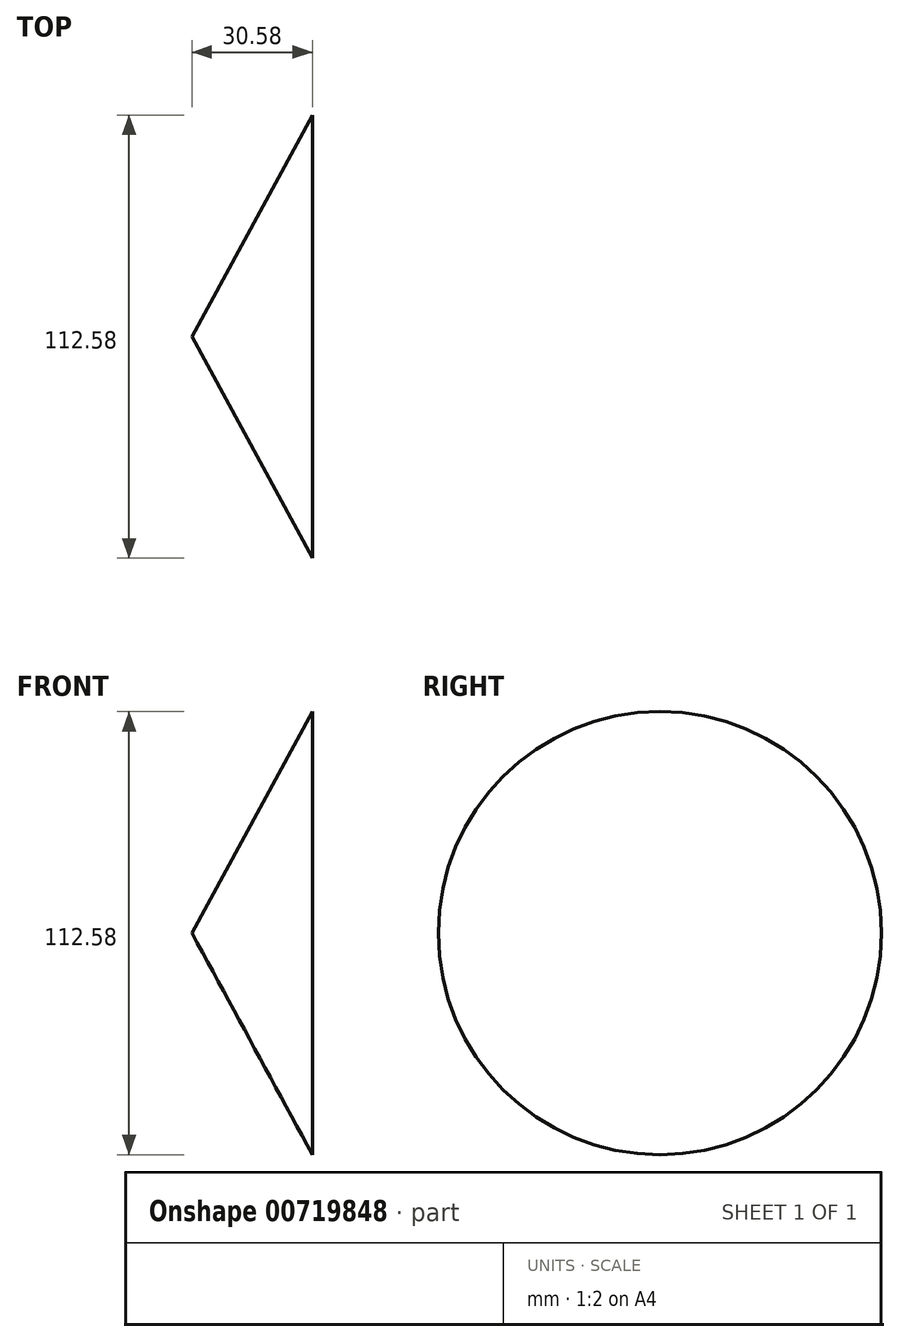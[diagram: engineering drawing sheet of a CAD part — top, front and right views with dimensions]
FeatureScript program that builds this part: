
annotation { "Feature Type Name" : "Feature", "Feature Type Description" : "" }
export const myFeature = defineFeature(function(context is Context, id is Id, definition is map)
    precondition{}
    {
        {
            var Q0;
            Q0=qCreatedBy(makeId("Front.planeOp"),FACE);
            var sketch = newSketch(context, id + "F0", { "sketchPlane" : qUnion([Q0])});
            skLineSegment(sketch, "E0", {"start": v(0, 56.3) * mm, "end": v(-30.58, 0) * mm});
            skLineSegment(sketch, "E1", {"start": v(-30.58, 0) * mm, "end": v(0, 0) * mm});
            skSolve(sketch);
        }
        {
            var Q0;
            Q0 = qSketchRegion(id + "F0", true);
            var Q1;
            Q1=sQuery(id+"F0.wireOp",EDGE,"E0");
            var Q2;
            Q2=sQuery(id+"F0.wireOp",EDGE,"E1");
            revolve(context, id + "F1", {"bodyType" : ToolBodyType.SURFACE, "surfaceOperationType" : NewSurfaceOperationType.NEW, "entities" : qUnion([Q0]), "surfaceEntities" : qUnion([Q1]), "axis" : qUnion([Q2]), "revolveType" : RevolveType.FULL});
        }
    });
